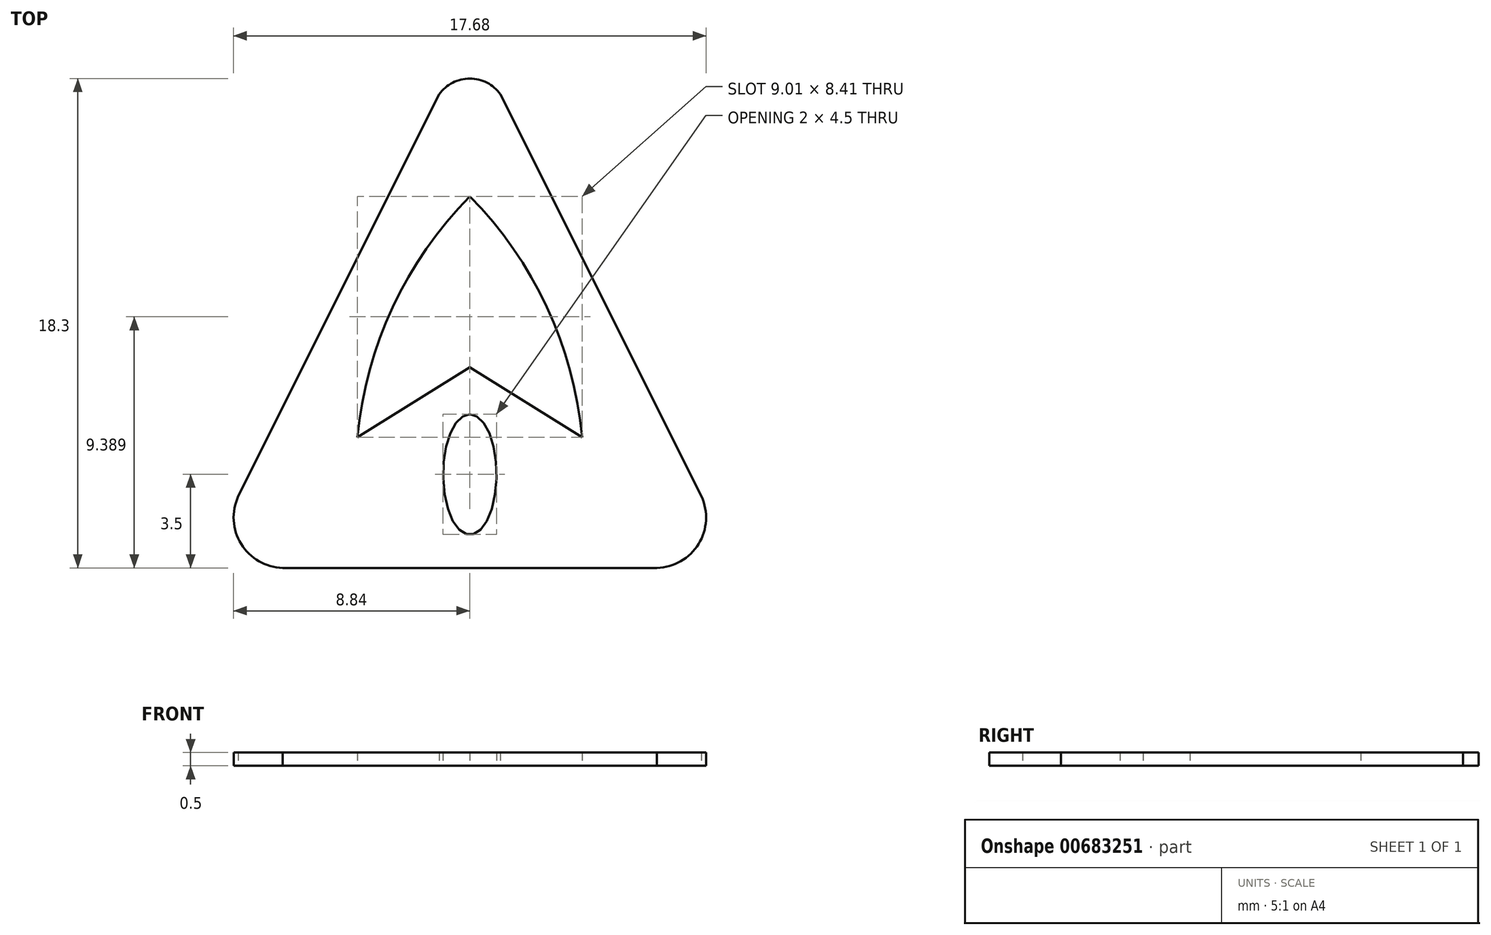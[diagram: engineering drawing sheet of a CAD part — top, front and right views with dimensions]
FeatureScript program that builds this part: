
annotation { "Feature Type Name" : "Feature", "Feature Type Description" : "" }
export const myFeature = defineFeature(function(context is Context, id is Id, definition is map)
    precondition{}
    {
        {
            var Q0;
            Q0=qCreatedBy(makeId("Top.planeOp"),FACE);
            var sketch = newSketch(context, id + "F0", { "sketchPlane" : qUnion([Q0])});
            skLineSegment(sketch, "E0", {"start": v(0, 20) * mm, "end": v(10, 0) * mm});
            skLineSegment(sketch, "E1", {"start": v(10, 0) * mm, "end": v(-10, 0) * mm});
            skLineSegment(sketch, "E2", {"start": v(-10, 0) * mm, "end": v(0, 20) * mm});
            skArc(sketch, "E3", {"start": v(1.34, 17.32) * mm, "mid": v(0, 18.3) * mm, "end": v(-1.34, 17.32) * mm});
            skArc(sketch, "E4", {"start": v(7, 0) * mm, "mid": v(8.55, 0.9) * mm, "end": v(8.66, 2.68) * mm});
            skArc(sketch, "E5", {"start": v(-8.66, 2.68) * mm, "mid": v(-8.55, 0.9) * mm, "end": v(-7, 0) * mm});
            skArc(sketch, "E6", {"start": v(4.2, 4.89) * mm, "mid": v(2.88, 9.75) * mm, "end": v(0, 13.9) * mm});
            skArc(sketch, "E7", {"start": v(0, 13.9) * mm, "mid": v(-2.88, 9.75) * mm, "end": v(-4.2, 4.89) * mm});
            skLineSegment(sketch, "E8", {"start": v(-4.2, 4.89) * mm, "end": v(0, 7.5) * mm});
            skLineSegment(sketch, "E9", {"start": v(0, 7.5) * mm, "end": v(4.2, 4.89) * mm});
            skEllipse(sketch, "E10", {"center": v(0, 3.5) * mm, "majorRadius": 2.25 * mm, "minorRadius": 1 * mm, "majorAxis": v(0, 1)});
            skSolve(sketch);
        }
        {
            var Q0;
            {var subQ1=sQuery(id+"F0.wireOp",EDGE,"E4");Q0=makeQuery(id+"F0.imprint","IMPRINT",FACE,{"disambiguationData":[TD([[makeQuery(id+"F0.imprint","IMPRINT",EDGE,{"derivedFrom":subQ1}),1.0]])]});}
            extrude(context, id + "F1", {"entities" : qUnion([Q0]), "depth" : 0.5 * mm, "offsetDistance" : 25 * mm});
        }
    });
